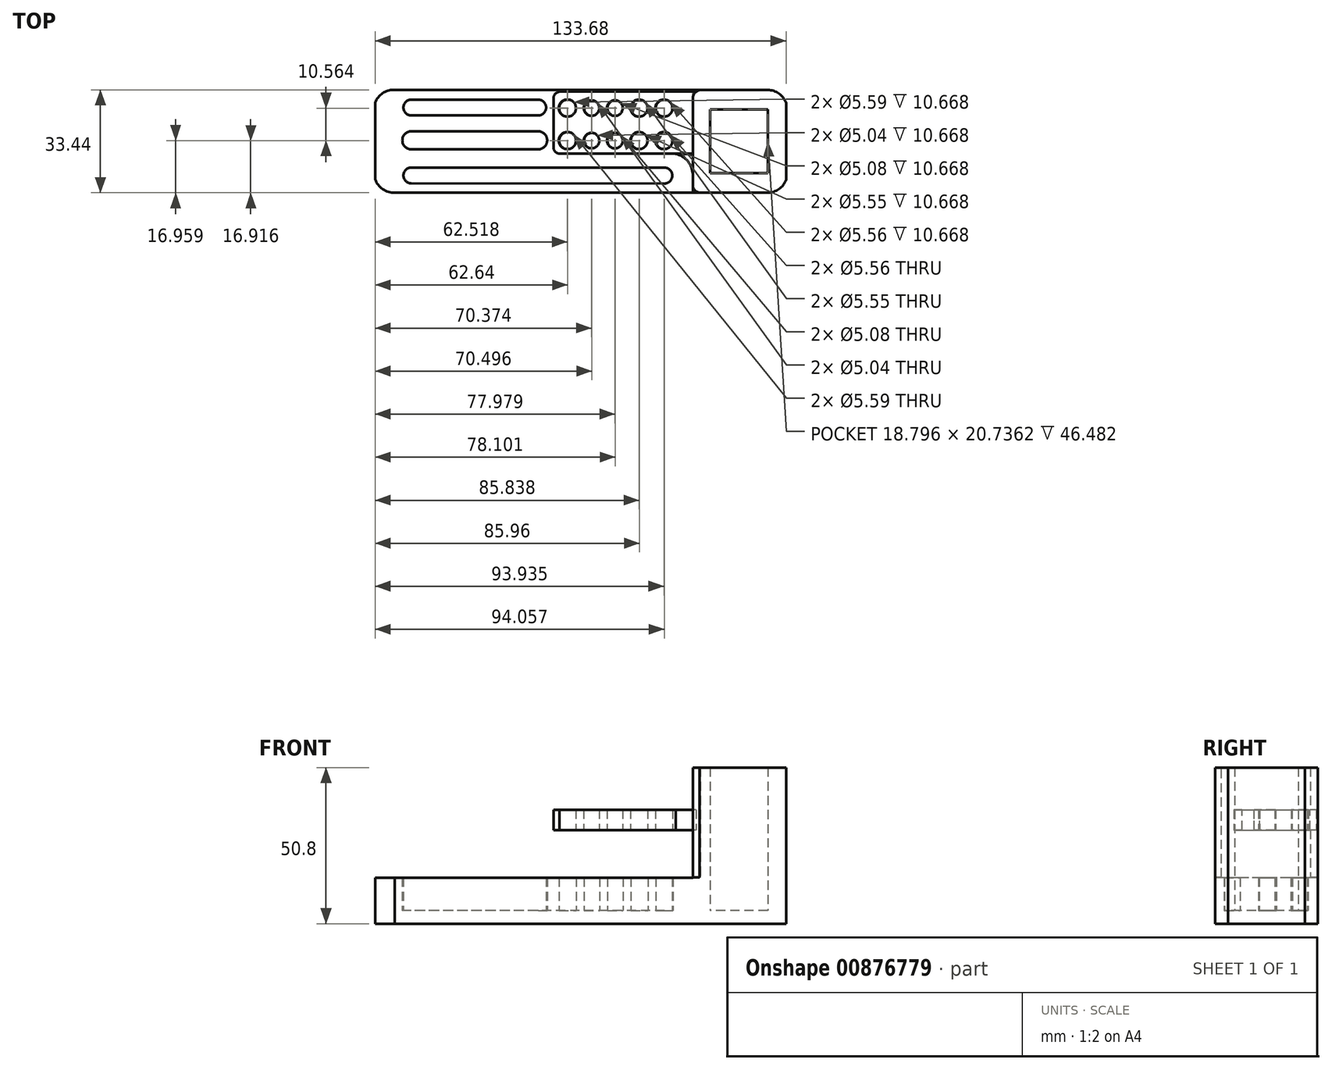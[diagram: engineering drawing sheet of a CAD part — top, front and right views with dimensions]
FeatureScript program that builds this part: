
annotation { "Feature Type Name" : "Feature", "Feature Type Description" : "" }
export const myFeature = defineFeature(function(context is Context, id is Id, definition is map)
    precondition{}
    {
        {
            var Q0;
            Q0=qCreatedBy(makeId("Top.planeOp"),FACE);
            var sketch = newSketch(context, id + "F0", { "sketchPlane" : qUnion([Q0])});
            skArc(sketch, "E0", {"start": v(41.75, -52.98) * mm, "mid": v(45.4, -51.83) * mm, "end": v(47.72, -48.8) * mm});
            skArc(sketch, "E1", {"start": v(47.72, -23.74) * mm, "mid": v(45.4, -20.71) * mm, "end": v(41.75, -19.56) * mm});
            skLineSegment(sketch, "E2", {"start": v(47.72, -48.8) * mm, "end": v(47.72, -23.74) * mm});
            skArc(sketch, "E3", {"start": v(22.95, -19.54) * mm, "mid": v(19.31, -20.69) * mm, "end": v(16.99, -23.72) * mm});
            skArc(sketch, "E4", {"start": v(16.99, -48.77) * mm, "mid": v(19.31, -51.8) * mm, "end": v(22.95, -52.95) * mm});
            skLineSegment(sketch, "E5", {"start": v(16.99, -23.72) * mm, "end": v(16.99, -48.77) * mm});
            skLineSegment(sketch, "E6", {"start": v(22.95, -25.9) * mm, "end": v(41.75, -25.91) * mm});
            skLineSegment(sketch, "E7", {"start": v(41.75, -46.63) * mm, "end": v(41.75, -25.91) * mm});
            skLineSegment(sketch, "E8", {"start": v(22.95, -46.6) * mm, "end": v(22.95, -25.9) * mm});
            skLineSegment(sketch, "E9", {"start": v(22.95, -46.6) * mm, "end": v(41.75, -46.63) * mm});
            skLineSegment(sketch, "E10", {"start": v(-74.22, -22.7) * mm, "end": v(-32.93, -22.71) * mm});
            skLineSegment(sketch, "E11", {"start": v(-74.22, -27.83) * mm, "end": v(-32.93, -27.84) * mm});
            skArc(sketch, "E12", {"start": v(-74.22, -22.7) * mm, "mid": v(-76.79, -25.27) * mm, "end": v(-74.22, -27.83) * mm});
            skArc(sketch, "E13", {"start": v(-32.93, -27.84) * mm, "mid": v(-30.37, -25.28) * mm, "end": v(-32.93, -22.71) * mm});
            skArc(sketch, "E14", {"start": v(-74.22, -44.82) * mm, "mid": v(-76.77, -47.37) * mm, "end": v(-74.22, -49.92) * mm});
            skLineSegment(sketch, "E15", {"start": v(-74.22, -33) * mm, "end": v(-32.93, -33.02) * mm});
            skLineSegment(sketch, "E16", {"start": v(-74.22, -38.87) * mm, "end": v(-32.93, -38.87) * mm});
            skArc(sketch, "E17", {"start": v(-74.22, -33) * mm, "mid": v(-77.15, -35.94) * mm, "end": v(-74.22, -38.87) * mm});
            skArc(sketch, "E18", {"start": v(-32.93, -38.87) * mm, "mid": v(-30, -35.95) * mm, "end": v(-32.93, -33.02) * mm});
            skCircle(sketch, "E19", {"center": v(8.1, -25.5) * mm, "radius": 2.78 * mm});
            skCircle(sketch, "E20", {"center": v(0, -25.5) * mm, "radius": 2.78 * mm});
            skCircle(sketch, "E21", {"center": v(-7.86, -25.5) * mm, "radius": 2.54 * mm});
            skCircle(sketch, "E22", {"center": v(-15.46, -25.5) * mm, "radius": 2.52 * mm});
            skCircle(sketch, "E23", {"center": v(-23.32, -25.5) * mm, "radius": 2.8 * mm});
            skLineSegment(sketch, "E24", {"start": v(-74.22, -44.82) * mm, "end": v(8.1, -44.82) * mm});
            skLineSegment(sketch, "E25", {"start": v(-74.22, -49.92) * mm, "end": v(8.1, -50.02) * mm});
            skArc(sketch, "E26", {"start": v(8.1, -50.02) * mm, "mid": v(10.7, -47.42) * mm, "end": v(8.1, -44.82) * mm});
            skCircle(sketch, "E27", {"center": v(8.1, -36.06) * mm, "radius": 2.78 * mm});
            skCircle(sketch, "E28", {"center": v(0, -36.06) * mm, "radius": 2.78 * mm});
            skCircle(sketch, "E29", {"center": v(-7.86, -36.06) * mm, "radius": 2.54 * mm});
            skCircle(sketch, "E30", {"center": v(-15.46, -36.06) * mm, "radius": 2.52 * mm});
            skCircle(sketch, "E31", {"center": v(-23.32, -36.06) * mm, "radius": 2.8 * mm});
            skArc(sketch, "E32", {"start": v(-79.98, -19.54) * mm, "mid": v(-83.6, -20.63) * mm, "end": v(-85.96, -23.58) * mm});
            skArc(sketch, "E33", {"start": v(-85.96, -48.64) * mm, "mid": v(-83.52, -51.85) * mm, "end": v(-79.64, -52.96) * mm});
            skLineSegment(sketch, "E34", {"start": v(-85.96, -23.58) * mm, "end": v(-85.96, -48.64) * mm});
            skLineSegment(sketch, "E35", {"start": v(-79.98, -19.54) * mm, "end": v(41.75, -19.56) * mm});
            skLineSegment(sketch, "E36", {"start": v(41.75, -52.98) * mm, "end": v(-79.64, -52.96) * mm});
            skSolve(sketch);
        }
        {
            var Q0;
            Q0 = qSketchRegion(id + "F0", true);
            extrude(context, id + "F1", {"entities" : qUnion([Q0]), "depth" : 50.8 * mm, "offsetDistance" : 25.4 * mm});
        }
        {
            var Q0;
            Q0=makeQuery(id+"F1.opExtrude","CAP_FACE",FACE,{"disambiguationData":[OSD([sQuery(id+"F0.wireOp",EDGE,"E0"),sQuery(id+"F0.wireOp",EDGE,"E1"),sQuery(id+"F0.wireOp",EDGE,"E2"),sQuery(id+"F0.wireOp",EDGE,"E6"),sQuery(id+"F0.wireOp",EDGE,"E7"),sQuery(id+"F0.wireOp",EDGE,"E8"),sQuery(id+"F0.wireOp",EDGE,"E9"),sQuery(id+"F0.wireOp",EDGE,"wLS4OOV2-Txmz-N7za-cG9D-8AIVijDkMkZu"),sQuery(id+"F0.wireOp",EDGE,"F14ueVxS-Sbc8-4dbj-0lzb-LM5rPNnnzRqA"),sQuery(id+"F0.wireOp",EDGE,"E10"),sQuery(id+"F0.wireOp",EDGE,"E11"),sQuery(id+"F0.wireOp",EDGE,"E12"),sQuery(id+"F0.wireOp",EDGE,"E13"),sQuery(id+"F0.wireOp",EDGE,"E14"),sQuery(id+"F0.wireOp",EDGE,"E15"),sQuery(id+"F0.wireOp",EDGE,"E16"),sQuery(id+"F0.wireOp",EDGE,"E17"),sQuery(id+"F0.wireOp",EDGE,"E18"),sQuery(id+"F0.wireOp",EDGE,"c2c865d6-f4c8-482e-8aa9-316942cdb41e"),sQuery(id+"F0.wireOp",EDGE,"739eb2a2-c741-4d6e-a7f9-82aa13231283"),sQuery(id+"F0.wireOp",EDGE,"a419fa84-276b-4bf7-8b8f-027718702883"),sQuery(id+"F0.wireOp",EDGE,"E19"),sQuery(id+"F0.wireOp",EDGE,"E20"),sQuery(id+"F0.wireOp",EDGE,"E21"),sQuery(id+"F0.wireOp",EDGE,"E22"),sQuery(id+"F0.wireOp",EDGE,"E23"),sQuery(id+"F0.wireOp",EDGE,"E24"),sQuery(id+"F0.wireOp",EDGE,"E25"),sQuery(id+"F0.wireOp",EDGE,"E26")])],"isStart":false});
            var sketch = newSketch(context, id + "F2", { "sketchPlane" : qUnion([Q0])});
            skLineSegment(sketch, "E37.bottom", {"start": v(-102.83, -7.68) * mm, "end": v(17.38, -7.68) * mm});
            skLineSegment(sketch, "E37.top", {"start": v(-102.83, -68.54) * mm, "end": v(17.38, -68.54) * mm});
            skLineSegment(sketch, "E37.left", {"start": v(-102.83, -7.68) * mm, "end": v(-102.83, -68.54) * mm});
            skLineSegment(sketch, "E37.right", {"start": v(17.38, -7.68) * mm, "end": v(17.38, -68.54) * mm});
            skSolve(sketch);
        }
        {
            var Q0;
            Q0 = qSketchRegion(id + "F2", true);
            extrude(context, id + "F3", {"entities" : qUnion([Q0]), "operationType" : NewBodyOperationType.REMOVE, "oppositeDirection" : true, "depth" : 35.81 * mm, "offsetDistance" : 25.4 * mm});
        }
        {
            var Q0;
            Q0=makeQuery(id+"F1.opExtrude","CAP_FACE",FACE,{"disambiguationData":[OSD([sQuery(id+"F0.wireOp",EDGE,"E0"),sQuery(id+"F0.wireOp",EDGE,"E1"),sQuery(id+"F0.wireOp",EDGE,"E2"),sQuery(id+"F0.wireOp",EDGE,"E6"),sQuery(id+"F0.wireOp",EDGE,"E7"),sQuery(id+"F0.wireOp",EDGE,"E8"),sQuery(id+"F0.wireOp",EDGE,"E9"),sQuery(id+"F0.wireOp",EDGE,"wLS4OOV2-Txmz-N7za-cG9D-8AIVijDkMkZu"),sQuery(id+"F0.wireOp",EDGE,"F14ueVxS-Sbc8-4dbj-0lzb-LM5rPNnnzRqA"),sQuery(id+"F0.wireOp",EDGE,"E10"),sQuery(id+"F0.wireOp",EDGE,"E11"),sQuery(id+"F0.wireOp",EDGE,"E12"),sQuery(id+"F0.wireOp",EDGE,"E13"),sQuery(id+"F0.wireOp",EDGE,"E14"),sQuery(id+"F0.wireOp",EDGE,"E15"),sQuery(id+"F0.wireOp",EDGE,"E16"),sQuery(id+"F0.wireOp",EDGE,"E17"),sQuery(id+"F0.wireOp",EDGE,"E18"),sQuery(id+"F0.wireOp",EDGE,"c2c865d6-f4c8-482e-8aa9-316942cdb41e"),sQuery(id+"F0.wireOp",EDGE,"739eb2a2-c741-4d6e-a7f9-82aa13231283"),sQuery(id+"F0.wireOp",EDGE,"a419fa84-276b-4bf7-8b8f-027718702883"),sQuery(id+"F0.wireOp",EDGE,"E19"),sQuery(id+"F0.wireOp",EDGE,"E20"),sQuery(id+"F0.wireOp",EDGE,"E21"),sQuery(id+"F0.wireOp",EDGE,"E22"),sQuery(id+"F0.wireOp",EDGE,"E23"),sQuery(id+"F0.wireOp",EDGE,"E24"),sQuery(id+"F0.wireOp",EDGE,"E25"),sQuery(id+"F0.wireOp",EDGE,"E26")])],"isStart":true});
            var sketch = newSketch(context, id + "F4", { "sketchPlane" : qUnion([Q0])});
            skLineSegment(sketch, "E38.bottom", {"start": v(-80.78, 51.1) * mm, "end": v(43.78, 51.1) * mm});
            skLineSegment(sketch, "E38.top", {"start": v(-80.78, 21.45) * mm, "end": v(43.78, 21.45) * mm});
            skLineSegment(sketch, "E38.left", {"start": v(-80.78, 51.1) * mm, "end": v(-80.78, 21.45) * mm});
            skLineSegment(sketch, "E38.right", {"start": v(43.78, 51.1) * mm, "end": v(43.78, 21.45) * mm});
            skSolve(sketch);
        }
        {
            var Q0;
            Q0 = qSketchRegion(id + "F4", true);
            extrude(context, id + "F5", {"entities" : qUnion([Q0]), "operationType" : NewBodyOperationType.ADD, "oppositeDirection" : true, "depth" : 4.32 * mm, "offsetDistance" : 25.4 * mm});
        }
        {
            var Q0;
            Q0=qCreatedBy(makeId("Top.planeOp"),FACE);
            cPlane(context, id + "F6", {"entities" : qUnion([Q0]), "cplaneType" : CPlaneType.OFFSET, "offset" : 33.78 * mm, "width" : 152.4 * mm, "height" : 152.4 * mm});
        }
        {
            var Q0;
            Q0=qCreatedBy(id+"F6.planeOp",FACE);
            var sketch = newSketch(context, id + "F7", { "sketchPlane" : qUnion([Q0])});
            skCircle(sketch, "E39", {"center": v(7.97, -25.46) * mm, "radius": 2.78 * mm});
            skCircle(sketch, "E40", {"center": v(-0.12, -25.46) * mm, "radius": 2.78 * mm});
            skCircle(sketch, "E41", {"center": v(-7.98, -25.46) * mm, "radius": 2.54 * mm});
            skCircle(sketch, "E42", {"center": v(-15.59, -25.46) * mm, "radius": 2.52 * mm});
            skCircle(sketch, "E43", {"center": v(-23.44, -25.46) * mm, "radius": 2.8 * mm});
            skCircle(sketch, "E44", {"center": v(7.97, -36.02) * mm, "radius": 2.78 * mm});
            skCircle(sketch, "E45", {"center": v(-0.12, -36.02) * mm, "radius": 2.78 * mm});
            skCircle(sketch, "E46", {"center": v(-7.98, -36.02) * mm, "radius": 2.54 * mm});
            skCircle(sketch, "E47", {"center": v(-15.59, -36.02) * mm, "radius": 2.52 * mm});
            skCircle(sketch, "E48", {"center": v(-23.44, -36.02) * mm, "radius": 2.8 * mm});
            skLineSegment(sketch, "E49.bottom", {"start": v(19.3, -40.3) * mm, "end": v(-27.99, -40.3) * mm});
            skLineSegment(sketch, "E49.top", {"start": v(19.35, -20.1) * mm, "end": v(-27.99, -20.1) * mm});
            skLineSegment(sketch, "E49.right", {"start": v(-27.99, -40.3) * mm, "end": v(-27.99, -20.1) * mm});
            skLineSegment(sketch, "E50.left", {"start": v(19.3, -20.1) * mm, "end": v(19.3, -40.3) * mm});
            skSolve(sketch);
        }
        {
            var Q0;
            Q0=qCreatedBy(makeId("Top.planeOp"),FACE);
            cPlane(context, id + "F8", {"entities" : qUnion([Q0]), "cplaneType" : CPlaneType.OFFSET, "offset" : 15.04 * mm, "width" : 152.4 * mm, "height" : 152.4 * mm});
        }
        {
            var Q0;
            Q0=qCreatedBy(id+"F8.planeOp",FACE);
            var sketch = newSketch(context, id + "F9", { "sketchPlane" : qUnion([Q0])});
            skArc(sketch, "E51", {"start": v(20.41, -19.56) * mm, "mid": v(18.4, -20.15) * mm, "end": v(17.38, -21.98) * mm});
            skLineSegment(sketch, "E52", {"start": v(17.38, -21.98) * mm, "end": v(17.38, -19.56) * mm});
            skLineSegment(sketch, "E53", {"start": v(17.38, -19.56) * mm, "end": v(20.41, -19.56) * mm});
            skSolve(sketch);
        }
        {
            var Q0;
            Q0 = qSketchRegion(id + "F9", true);
            extrude(context, id + "F10", {"entities" : qUnion([Q0]), "operationType" : NewBodyOperationType.REMOVE, "depth" : 91.7 * mm, "offsetDistance" : 25.4 * mm});
        }
        {
            var Q0;
            Q0 = qSketchRegion(id + "F7", true);
            extrude(context, id + "F11", {"entities" : qUnion([Q0]), "operationType" : NewBodyOperationType.ADD, "endBound" : BoundingType.SYMMETRIC, "depth" : 6.6 * mm, "offsetDistance" : 25.4 * mm});
        }
        {
            var Q0;
            Q0=makeQuery(id+"F11.opExtrude","CAP_FACE",FACE,{"disambiguationData":[OSD([sQuery(id+"F7.wireOp",EDGE,"E39"),sQuery(id+"F7.wireOp",EDGE,"E40"),sQuery(id+"F7.wireOp",EDGE,"E41"),sQuery(id+"F7.wireOp",EDGE,"E42"),sQuery(id+"F7.wireOp",EDGE,"E43"),sQuery(id+"F7.wireOp",EDGE,"E44"),sQuery(id+"F7.wireOp",EDGE,"E45"),sQuery(id+"F7.wireOp",EDGE,"E46"),sQuery(id+"F7.wireOp",EDGE,"E47"),sQuery(id+"F7.wireOp",EDGE,"E48"),sQuery(id+"F7.wireOp",EDGE,"E49.bottom"),sQuery(id+"F7.wireOp",EDGE,"E49.top"),sQuery(id+"F7.wireOp",EDGE,"E49.right"),sQuery(id+"F7.wireOp",EDGE,"E50.left")])],"isStart":false});
            var sketch = newSketch(context, id + "F12", { "sketchPlane" : qUnion([Q0])});
            skArc(sketch, "E54", {"start": v(-25.77, -20.1) * mm, "mid": v(-27.45, -20.92) * mm, "end": v(-27.99, -22.7) * mm});
            skLineSegment(sketch, "E55", {"start": v(-27.99, -22.7) * mm, "end": v(-27.99, -20.1) * mm});
            skLineSegment(sketch, "E56", {"start": v(-27.99, -20.1) * mm, "end": v(-25.77, -20.1) * mm});
            skArc(sketch, "E57", {"start": v(-28.04, -38.09) * mm, "mid": v(-27.22, -39.77) * mm, "end": v(-25.43, -40.3) * mm});
            skLineSegment(sketch, "E58", {"start": v(-25.43, -40.3) * mm, "end": v(-28.04, -40.3) * mm});
            skLineSegment(sketch, "E59", {"start": v(-28.04, -40.3) * mm, "end": v(-28.04, -38.09) * mm});
            skSolve(sketch);
        }
        {
            var Q0;
            Q0 = qSketchRegion(id + "F12", true);
            extrude(context, id + "F13", {"entities" : qUnion([Q0]), "operationType" : NewBodyOperationType.REMOVE, "oppositeDirection" : true, "depth" : 13.44 * mm, "offsetDistance" : 25.4 * mm});
        }
        {
            var Q0;
            Q0=makeQuery(id+"F1.opExtrude","CAP_FACE",FACE,{"disambiguationData":[OSD([sQuery(id+"F0.wireOp",EDGE,"E0"),sQuery(id+"F0.wireOp",EDGE,"E1"),sQuery(id+"F0.wireOp",EDGE,"E2"),sQuery(id+"F0.wireOp",EDGE,"E6"),sQuery(id+"F0.wireOp",EDGE,"E7"),sQuery(id+"F0.wireOp",EDGE,"E8"),sQuery(id+"F0.wireOp",EDGE,"E9"),sQuery(id+"F0.wireOp",EDGE,"wLS4OOV2-Txmz-N7za-cG9D-8AIVijDkMkZu"),sQuery(id+"F0.wireOp",EDGE,"F14ueVxS-Sbc8-4dbj-0lzb-LM5rPNnnzRqA"),sQuery(id+"F0.wireOp",EDGE,"E10"),sQuery(id+"F0.wireOp",EDGE,"E11"),sQuery(id+"F0.wireOp",EDGE,"E12"),sQuery(id+"F0.wireOp",EDGE,"E13"),sQuery(id+"F0.wireOp",EDGE,"E14"),sQuery(id+"F0.wireOp",EDGE,"E15"),sQuery(id+"F0.wireOp",EDGE,"E16"),sQuery(id+"F0.wireOp",EDGE,"E17"),sQuery(id+"F0.wireOp",EDGE,"E18"),sQuery(id+"F0.wireOp",EDGE,"c2c865d6-f4c8-482e-8aa9-316942cdb41e"),sQuery(id+"F0.wireOp",EDGE,"739eb2a2-c741-4d6e-a7f9-82aa13231283"),sQuery(id+"F0.wireOp",EDGE,"a419fa84-276b-4bf7-8b8f-027718702883"),sQuery(id+"F0.wireOp",EDGE,"E19"),sQuery(id+"F0.wireOp",EDGE,"E20"),sQuery(id+"F0.wireOp",EDGE,"E21"),sQuery(id+"F0.wireOp",EDGE,"E22"),sQuery(id+"F0.wireOp",EDGE,"E23"),sQuery(id+"F0.wireOp",EDGE,"E24"),sQuery(id+"F0.wireOp",EDGE,"E25"),sQuery(id+"F0.wireOp",EDGE,"E26"),sQuery(id+"F0.wireOp",EDGE,"E27"),sQuery(id+"F0.wireOp",EDGE,"E28"),sQuery(id+"F0.wireOp",EDGE,"E29"),sQuery(id+"F0.wireOp",EDGE,"E30"),sQuery(id+"F0.wireOp",EDGE,"E31")])],"isStart":false});
            var sketch = newSketch(context, id + "F14", { "sketchPlane" : qUnion([Q0])});
            skArc(sketch, "E60", {"start": v(17.38, -50.92) * mm, "mid": v(18.32, -52.47) * mm, "end": v(20.06, -52.97) * mm});
            skLineSegment(sketch, "E61", {"start": v(17.38, -50.92) * mm, "end": v(17.38, -52.97) * mm});
            skLineSegment(sketch, "E62", {"start": v(17.38, -52.97) * mm, "end": v(20.06, -52.97) * mm});
            skSolve(sketch);
        }
        {
            var Q0;
            Q0 = qSketchRegion(id + "F14", true);
            extrude(context, id + "F15", {"entities" : qUnion([Q0]), "operationType" : NewBodyOperationType.REMOVE, "oppositeDirection" : true, "depth" : 35.7 * mm, "offsetDistance" : 25.4 * mm});
        }
        {
            var Q0;
            Q0=qCreatedBy(id+"F6.planeOp",FACE);
            var sketch = newSketch(context, id + "F16", { "sketchPlane" : qUnion([Q0])});
            skArc(sketch, "E63", {"start": v(17.36, -46.91) * mm, "mid": v(15.7, -42.72) * mm, "end": v(11.86, -40.35) * mm});
            skLineSegment(sketch, "E64", {"start": v(11.86, -40.35) * mm, "end": v(17.4, -40.35) * mm});
            skLineSegment(sketch, "E65", {"start": v(17.4, -40.35) * mm, "end": v(17.36, -46.91) * mm});
            skSolve(sketch);
        }
        {
            var Q0;
            Q0 = qSketchRegion(id + "F16", true);
            extrude(context, id + "F17", {"entities" : qUnion([Q0]), "operationType" : NewBodyOperationType.ADD, "endBound" : BoundingType.SYMMETRIC, "depth" : 6.6 * mm, "offsetDistance" : 25.4 * mm});
        }
    });
